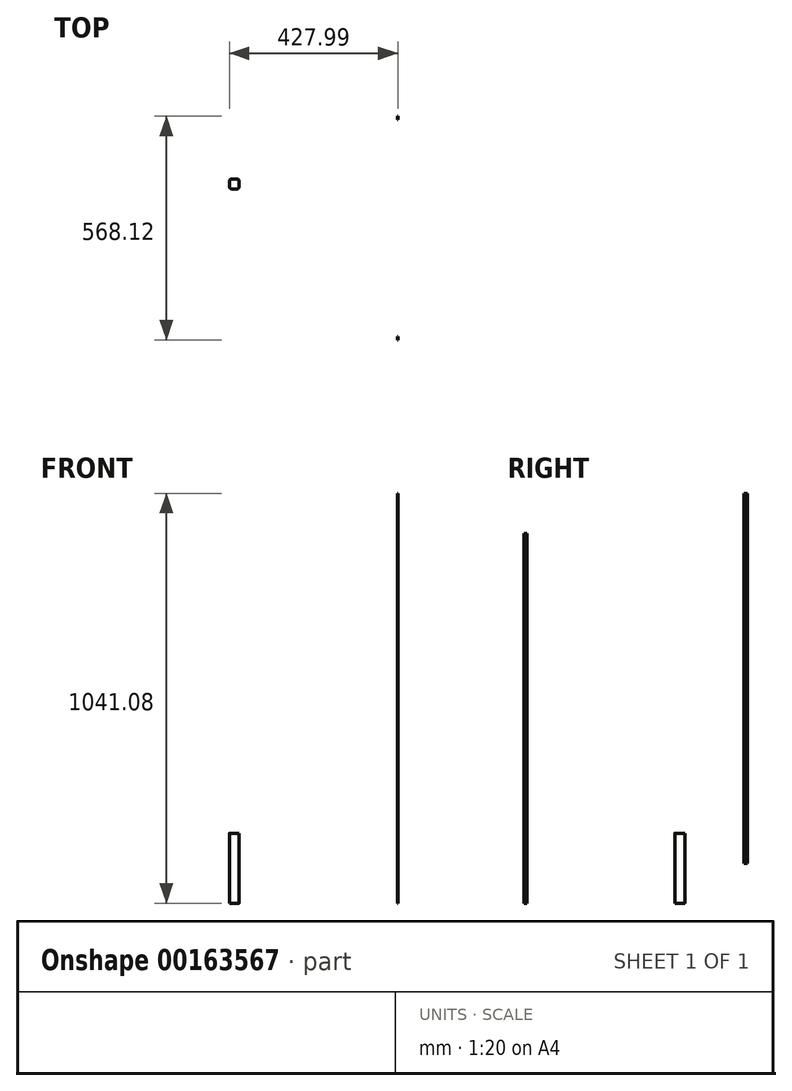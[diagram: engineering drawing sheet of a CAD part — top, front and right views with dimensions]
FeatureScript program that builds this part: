
annotation { "Feature Type Name" : "Feature", "Feature Type Description" : "" }
export const myFeature = defineFeature(function(context is Context, id is Id, definition is map)
    precondition{}
    {
        {
            var Q0;
            Q0=qCreatedBy(makeId("Top.planeOp"),FACE);
            var sketch = newSketch(context, id + "F0", { "sketchPlane" : qUnion([Q0])});
            skLineSegment(sketch, "E0.bottom", {"start": v(6.35, 12.7) * mm, "end": v(-6.35, 12.7) * mm});
            skLineSegment(sketch, "E0.top", {"start": v(6.35, -12.7) * mm, "end": v(-6.35, -12.7) * mm});
            skLineSegment(sketch, "E0.left", {"start": v(12.7, 6.35) * mm, "end": v(12.7, -6.35) * mm});
            skLineSegment(sketch, "E0.right", {"start": v(-12.7, 6.35) * mm, "end": v(-12.7, -6.35) * mm});
            skPoint(sketch, "E0.middle", {"position": v(0, 0) * mm});
            skPoint(sketch, "E1.visualSharp", {"position": v(-12.7, 12.7) * mm});
            skArc(sketch, "E1.filletArc", {"start": v(-6.35, 12.7) * mm, "mid": v(-10.84, 10.84) * mm, "end": v(-12.7, 6.35) * mm});
            skPoint(sketch, "E2.visualSharp", {"position": v(-12.7, -12.7) * mm});
            skArc(sketch, "E2.filletArc", {"start": v(-12.7, -6.35) * mm, "mid": v(-10.84, -10.84) * mm, "end": v(-6.35, -12.7) * mm});
            skPoint(sketch, "E3.visualSharp", {"position": v(12.7, -12.7) * mm});
            skArc(sketch, "E3.filletArc", {"start": v(6.35, -12.7) * mm, "mid": v(10.84, -10.84) * mm, "end": v(12.7, -6.35) * mm});
            skPoint(sketch, "E4.visualSharp", {"position": v(12.7, 12.7) * mm});
            skArc(sketch, "E4.filletArc", {"start": v(12.7, 6.35) * mm, "mid": v(10.84, 10.84) * mm, "end": v(6.35, 12.7) * mm});
            skSolve(sketch);
        }
        {
            var Q0;
            Q0=qSketchRegion(id+"F0",true);
            extrude(context, id + "F1", {"entities" : qUnion([Q0]), "depth" : 177.8 * mm, "offsetDistance" : 25.4 * mm});
        }
        {
            var Q0;
            Q0=qCreatedBy(makeId("Right.planeOp"),FACE);
            var sketch = newSketch(context, id + "F2", { "sketchPlane" : qUnion([Q0])});
            skLineSegment(sketch, "E5.bottom", {"start": v(-396.35, 939.8) * mm, "end": v(-387.88, 939.8) * mm});
            skLineSegment(sketch, "E5.top", {"start": v(-396.35, 0) * mm, "end": v(-387.88, 0) * mm});
            skLineSegment(sketch, "E5.left", {"start": v(-396.35, 939.8) * mm, "end": v(-396.35, 0) * mm});
            skLineSegment(sketch, "E5.right", {"start": v(-387.88, 939.8) * mm, "end": v(-387.88, 0) * mm});
            skSolve(sketch);
        }
        {
            var Q0;
            Q0=qSketchRegion(id+"F2",true);
            extrude(context, id + "F3", {"entities" : qUnion([Q0]), "depth" : 1.27 * mm});
        }
        {
            var Q0;
            Q0=qCreatedBy(makeId("Right.planeOp"),FACE);
            var sketch = newSketch(context, id + "F4", { "sketchPlane" : qUnion([Q0])});
            skLineSegment(sketch, "E6.bottom", {"start": v(163.3, 1041.08) * mm, "end": v(171.77, 1041.08) * mm});
            skLineSegment(sketch, "E6.top", {"start": v(163.3, 101.28) * mm, "end": v(171.77, 101.28) * mm});
            skLineSegment(sketch, "E6.left", {"start": v(163.3, 1041.08) * mm, "end": v(163.3, 101.28) * mm});
            skLineSegment(sketch, "E6.right", {"start": v(171.77, 1041.08) * mm, "end": v(171.77, 101.28) * mm});
            skSolve(sketch);
        }
        {
            var Q0;
            Q0=qSketchRegion(id+"F4",true);
            extrude(context, id + "F5", {"entities" : qUnion([Q0]), "depth" : 1.27 * mm});
        }
        {
            var Q0;
            Q0=makeQuery(id+"F5.opExtrude","SWEPT_BODY",BODY,{"disambiguationData":[OSD([sQuery(id+"F4.wireOp",EDGE,"E6.bottom"),sQuery(id+"F4.wireOp",EDGE,"E6.top"),sQuery(id+"F4.wireOp",EDGE,"E6.left"),sQuery(id+"F4.wireOp",EDGE,"E6.right")])]});
            var Q1;
            Q1=makeQuery(id+"F3.opExtrude","SWEPT_BODY",BODY,{"disambiguationData":[OSD([sQuery(id+"F2.wireOp",EDGE,"E5.bottom"),sQuery(id+"F2.wireOp",EDGE,"E5.top"),sQuery(id+"F2.wireOp",EDGE,"E5.left"),sQuery(id+"F2.wireOp",EDGE,"E5.right")])]});
            transform(context, id + "F6", {"entities" : qUnion([Q0, Q1]), "transformType" : TransformType.TRANSLATION_3D, "dx" : 414.02 * mm, "dy" : 0 * mm, "dz" : 0 * mm, "makeCopy" : false});
        }
    });
